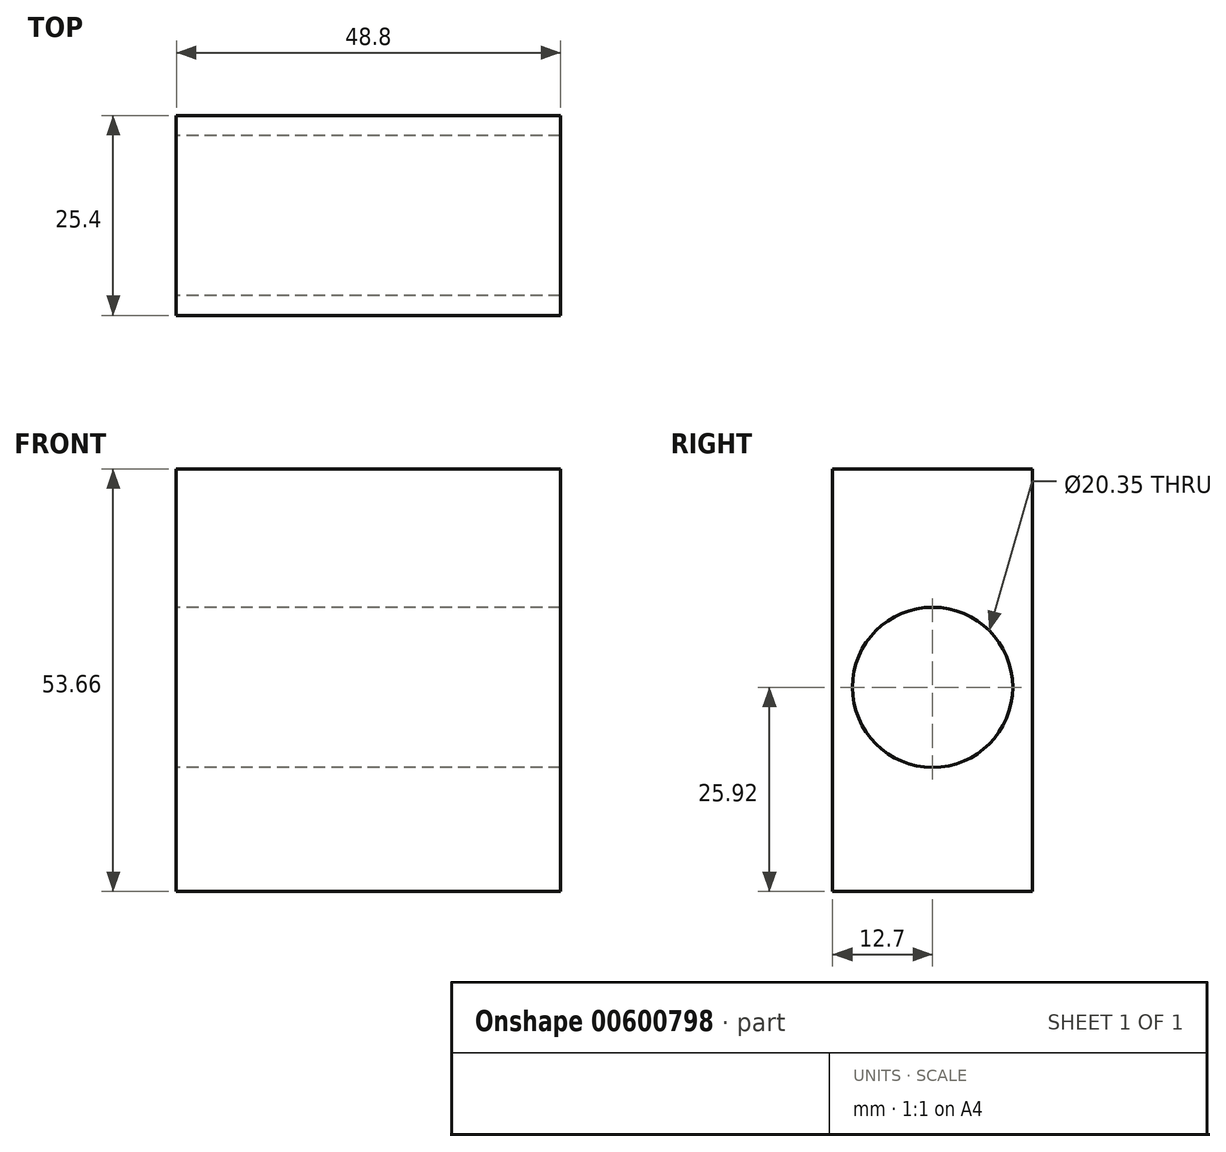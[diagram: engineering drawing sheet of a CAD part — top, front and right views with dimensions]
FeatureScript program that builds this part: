
annotation { "Feature Type Name" : "Feature", "Feature Type Description" : "" }
export const myFeature = defineFeature(function(context is Context, id is Id, definition is map)
    precondition{}
    {
        {
            var Q0;
            Q0=qCreatedBy(makeId("Front.planeOp"),FACE);
            var sketch = newSketch(context, id + "F0", { "sketchPlane" : qUnion([Q0])});
            skLineSegment(sketch, "E0.bottom", {"start": v(-19.24, 27.74) * mm, "end": v(29.56, 27.74) * mm});
            skLineSegment(sketch, "E0.top", {"start": v(-19.24, -25.92) * mm, "end": v(29.56, -25.92) * mm});
            skLineSegment(sketch, "E0.left", {"start": v(-19.24, 27.74) * mm, "end": v(-19.24, -25.92) * mm});
            skLineSegment(sketch, "E0.right", {"start": v(29.56, 27.74) * mm, "end": v(29.56, -25.92) * mm});
            skSolve(sketch);
        }
        {
            var Q0;
            Q0 = qSketchRegion(id + "F0", true);
            extrude(context, id + "F1", {"entities" : qUnion([Q0]), "endBound" : BoundingType.SYMMETRIC, "depth" : 25.4 * mm, "offsetDistance" : 25.4 * mm});
        }
        {
            var Q0;
            Q0=qCreatedBy(makeId("Right.planeOp"),FACE);
            var sketch = newSketch(context, id + "F2", { "sketchPlane" : qUnion([Q0])});
            skCircle(sketch, "E1", {"center": v(0, 0) * mm, "radius": 10.18 * mm});
            skSolve(sketch);
        }
        {
            var Q0;
            Q0 = qSketchRegion(id + "F2", true);
            extrude(context, id + "F3", {"entities" : qUnion([Q0]), "operationType" : NewBodyOperationType.REMOVE, "endBound" : BoundingType.SYMMETRIC, "depth" : 74.68 * mm, "offsetDistance" : 25.4 * mm});
        }
    });
